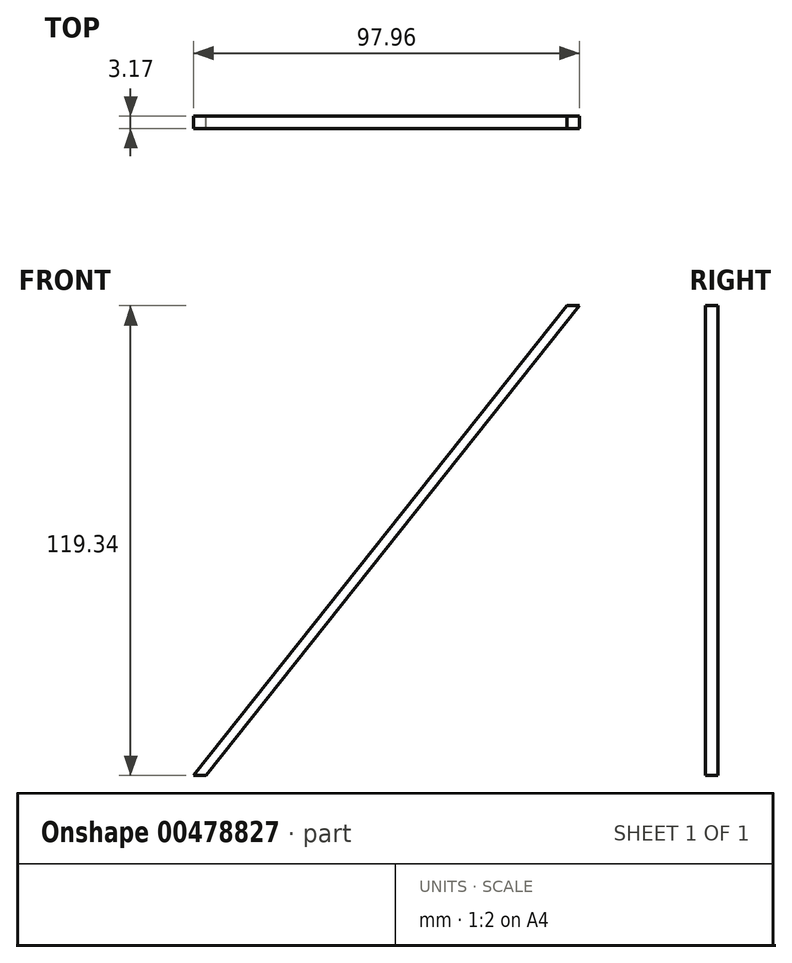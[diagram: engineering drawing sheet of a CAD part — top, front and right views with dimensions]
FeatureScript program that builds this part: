
annotation { "Feature Type Name" : "Feature", "Feature Type Description" : "" }
export const myFeature = defineFeature(function(context is Context, id is Id, definition is map)
    precondition{}
    {
        {
            var Q0;
            Q0=qCreatedBy(makeId("Front.planeOp"),FACE);
            var sketch = newSketch(context, id + "F0", { "sketchPlane" : qUnion([Q0])});
            skLineSegment(sketch, "E0", {"start": v(-112.3, 0) * mm, "end": v(-17.51, 119.34) * mm});
            skLineSegment(sketch, "E1", {"start": v(-17.51, 119.34) * mm, "end": v(-14.34, 119.34) * mm});
            skLineSegment(sketch, "E2", {"start": v(-14.34, 119.34) * mm, "end": v(-109.12, 0) * mm});
            skLineSegment(sketch, "E3", {"start": v(-109.12, 0) * mm, "end": v(-112.3, 0) * mm});
            skSolve(sketch);
        }
        {
            var Q0;
            Q0=makeQuery(id+"F0.imprint","IMPRINT",FACE,{"disambiguationData":[TD([[makeQuery(id+"F0.imprint","IMPRINT",EDGE,{"derivedFrom":sQuery(id+"F0.wireOp",EDGE,"E0")}),-1.0]])]});
            extrude(context, id + "F1", {"entities" : qUnion([Q0]), "depth" : 3.17 * mm});
        }
    });
